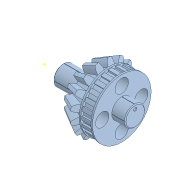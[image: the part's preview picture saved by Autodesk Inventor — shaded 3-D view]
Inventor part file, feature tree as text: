
AUTODESK INVENTOR PART (.ipt)
format: ipt  version: 2022.5 (Build 265521000, 521)  size: 513,024 bytes
history: native  units: in
note: dims shown in document units (in); Inventor stores cm internally (conversion verified against a paired STEP export)
features: sketch x11, extrude x8, plane x6, pattern_circular x3, revolve x2, chamfer x1
ambient origin geometry x8: Origin, YZ Plane, XZ Plane, XY Plane, X Axis, Y Axis, Z Axis, Center Point
bodies: Solid1 (feature_tree)
feature tree (31):
  revolve  "Revolution1"  [1 undecoded]
  plane  "Work Plane2"
  plane  "Work Plane5"
  extrude  "Extrusion6"  Depth=0.0945in
  pattern_circular  "Circular Pattern2"  Count=4  [1 undecoded]
  plane  "Work Plane7"
  extrude  "Extrusion7"  Depth=0.162in
  plane  "Work Plane6"
  sketch  "Sketch11"  dims[d10=90.0deg d11=0.162in d12=1.5748in]
  revolve  "Revolution3"  [1 undecoded]
  extrude  "Extrusion8"  Depth=0.3543in
  extrude  "Extrusion9"  Depth=0.0787in
  pattern_circular  "Circular Pattern3"  Count=16 Angle=360.0deg
  chamfer  "Chamfer3"  Distance=0.0787in
  extrude  "Extrusion10"  Depth=0.1575in
  extrude  "Extrusion11"  Depth=0.3937in TaperAngle=0.0deg
  extrude  "Extrusion12"  Depth=0.3937in
  extrude  "Extrusion13"  [1 undecoded]
  pattern_circular  "Circular Pattern4"  [2 undecoded]
  sketch  "Sketch1"  dims[d0=3.1496in d1=0.1825in]
  plane  "Work Plane1"
  plane  "Work Plane4"
  sketch  "Sketch8"  dims[d2=0.0787in d3=0.0945in]
  sketch  "Sketch10"  dims[d5=0.3937in d9=1.5748in]
  sketch  "Sketch12"  dims[d43=0.7043in d47=1.4085in]
  sketch  "Sketch13"  dims[d48=1.4961in d49=0.3543in]
  sketch  "Sketch14"  dims[d50=-0.4359in d51=1.5748in d53=0.0787in]
  sketch  "Sketch15"  dims[d54=0.0691in]
  sketch  "Sketch16"  dims[d56=0.4724in d57=-0.0197in d58=6.2992in d59=360.0deg]
  sketch  "Sketch17"  dims[d63=0.1297in]
  sketch  "Sketch18"  dims[d73=0.1575in d74=0.0787in d75=0.1575in d76=0.5906in d77=0.0in d82=0.0875in d83=-0.0875in d84=1.4086in d86=0.0394in d87=0.2362in d88=0.0591in d89=0.315in d90=0.315in d91=0.1181in d92=90.0deg d93=0.4724in d94=0.5906in d95=0.0in d96=0.2362in d97=0.6299in d98=0.0394in d99=0.0515in d100=0.3937in d101=0.0in d102=9.4488in d103=360.0deg d105=0.0197in d106=0.0787in d107=45.0deg d108=0.1378in d109=0.0787in d110=0.0197in d111=0.0in d112=0.0079in d113=0.3937in d114=0.0in d115=0.0079in d116=0.3937in d117=0.0in d118=0.315in d119=0.315in d120=0.0in d121=1.5748in d122=360.0deg]
note: 6 required parameter values undecoded (feature->parameter linkage not recoverable at this tier; creation-order binding heuristic only, values carry confidence <= 0.55)